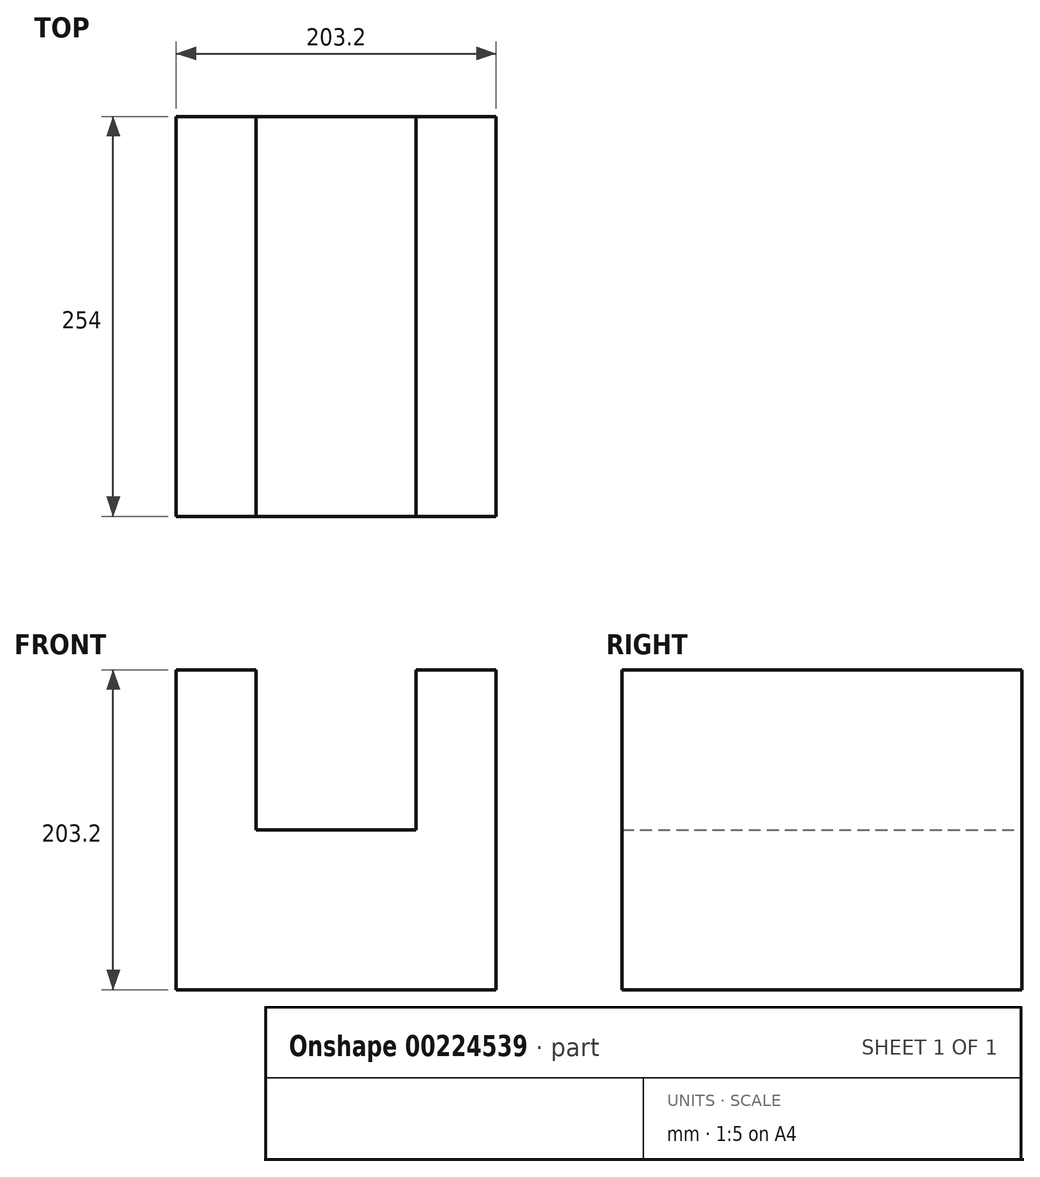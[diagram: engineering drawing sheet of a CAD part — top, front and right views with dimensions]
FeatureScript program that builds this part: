
annotation { "Feature Type Name" : "Feature", "Feature Type Description" : "" }
export const myFeature = defineFeature(function(context is Context, id is Id, definition is map)
    precondition{}
    {
        {
            var Q0;
            Q0=qCreatedBy(makeId("Front.planeOp"),FACE);
            var sketch = newSketch(context, id + "F0", { "sketchPlane" : qUnion([Q0])});
            skLineSegment(sketch, "E0.top", {"start": v(-152.4, -7.6) * mm, "end": v(50.8, -7.6) * mm});
            skLineSegment(sketch, "E0.left", {"start": v(-152.4, 195.6) * mm, "end": v(-152.4, -7.6) * mm});
            skLineSegment(sketch, "E0.right", {"start": v(50.8, 195.6) * mm, "end": v(50.8, -7.6) * mm});
            skLineSegment(sketch, "E1", {"start": v(-101.6, 195.6) * mm, "end": v(-101.6, 94) * mm});
            skLineSegment(sketch, "E2", {"start": v(-101.6, 94) * mm, "end": v(0, 94) * mm});
            skLineSegment(sketch, "E3", {"start": v(0, 94) * mm, "end": v(0, 195.6) * mm});
            skLineSegment(sketch, "E4", {"start": v(-152.4, 195.6) * mm, "end": v(-101.6, 195.6) * mm});
            skLineSegment(sketch, "E5", {"start": v(0, 195.6) * mm, "end": v(50.8, 195.6) * mm});
            skSolve(sketch);
        }
        {
            var Q0;
            Q0=makeQuery(id+"F0.imprint","IMPRINT",FACE,{"disambiguationData":[TD([[makeQuery(id+"F0.imprint","IMPRINT",EDGE,{"derivedFrom":sQuery(id+"F0.wireOp",EDGE,"E0.top")}),1.0]])]});
            extrude(context, id + "F1", {"entities" : qUnion([Q0]), "depth" : 254 * mm});
        }
    });
